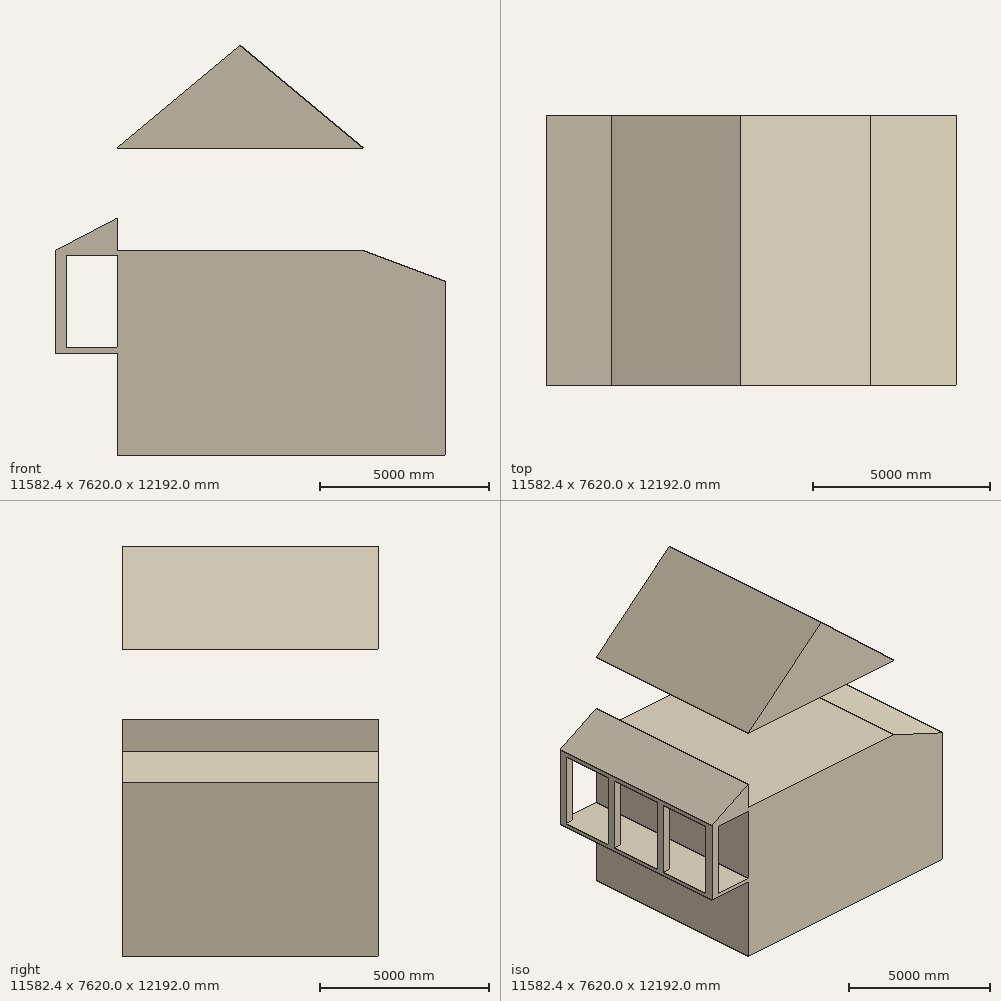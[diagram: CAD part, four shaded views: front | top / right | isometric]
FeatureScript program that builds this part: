
annotation { "Feature Type Name" : "Feature", "Feature Type Description" : "" }
export const myFeature = defineFeature(function(context is Context, id is Id, definition is map)
    precondition{}
    {
        {
            var Q0;
            Q0=qCreatedBy(makeId("Front.planeOp"),FACE);
            var sketch = newSketch(context, id + "F0", { "sketchPlane" : qUnion([Q0])});
            skLineSegment(sketch, "E0.bottom", {"start": v(0, 0) * mm, "end": v(-9753.6, 0) * mm});
            skLineSegment(sketch, "E0.top", {"start": v(0, 3048) * mm, "end": v(-9753.6, 3048) * mm});
            skLineSegment(sketch, "E0.left", {"start": v(0, 0) * mm, "end": v(0, 3048) * mm});
            skLineSegment(sketch, "E0.right", {"start": v(-9753.6, 0) * mm, "end": v(-9753.6, 3048) * mm});
            skLineSegment(sketch, "E1.bottom", {"start": v(0, 3048) * mm, "end": v(-11582.4, 3048) * mm});
            skLineSegment(sketch, "E1.top", {"start": v(-2438.33, 6096) * mm, "end": v(-9753.6, 6096) * mm});
            skLineSegment(sketch, "E1.left", {"start": v(0, 3048) * mm, "end": v(0, 5181.6) * mm});
            skLineSegment(sketch, "E1.right", {"start": v(-11582.4, 3048) * mm, "end": v(-11582.4, 6096) * mm});
            skLineSegment(sketch, "E2", {"start": v(0, 5181.6) * mm, "end": v(-2438.33, 6096) * mm});
            skLineSegment(sketch, "E3.bottom", {"start": v(-9753.6, 6096) * mm, "end": v(-2438.33, 6096) * mm});
            skLineSegment(sketch, "E3.top", {"start": v(-9753.6, 9144) * mm, "end": v(-2438.33, 9144) * mm});
            skLineSegment(sketch, "E3.left", {"start": v(-9753.6, 6096) * mm, "end": v(-9753.6, 9144) * mm});
            skLineSegment(sketch, "E3.right", {"start": v(-2438.33, 6096) * mm, "end": v(-2438.33, 9144) * mm});
            skLineSegment(sketch, "E4", {"start": v(-6095.96, 9144) * mm, "end": v(-6095.96, 12192) * mm});
            skLineSegment(sketch, "E5", {"start": v(-6095.96, 12192) * mm, "end": v(-2438.33, 9144) * mm});
            skLineSegment(sketch, "E6", {"start": v(-6095.96, 12192) * mm, "end": v(-9753.6, 9144) * mm});
            skLineSegment(sketch, "E7", {"start": v(-2438.33, 6096) * mm, "end": v(-2438.33, 6096) * mm});
            skLineSegment(sketch, "E8", {"start": v(-9753.6, 6096) * mm, "end": v(-11582.4, 6096) * mm});
            skLineSegment(sketch, "E9", {"start": v(-9753.6, 6096) * mm, "end": v(-9753.6, 7052.47) * mm});
            skLineSegment(sketch, "E10", {"start": v(-9753.6, 7052.47) * mm, "end": v(-11582.4, 6096) * mm});
            skSolve(sketch);
        }
        {
            var Q0;
            {var subQ2=sQuery(id+"F0.wireOp",EDGE,"E4");Q0=makeQuery(id+"F0.imprint","IMPRINT",FACE,{"disambiguationData":[TD([[makeQuery(id+"F0.imprint","IMPRINT",EDGE,{"derivedFrom":subQ2}),1.0]])]});}
            var Q1;
            Q1=makeQuery(id+"F0.imprint","IMPRINT",FACE,{"disambiguationData":[TD([[makeQuery(id+"F0.imprint","IMPRINT",EDGE,{"derivedFrom":sQuery(id+"F0.wireOp",EDGE,"E3.bottom")}),1.0]])]});
            var Q2;
            {var subQ1=sQuery(id+"F0.wireOp",EDGE,"E1.left");Q2=makeQuery(id+"F0.imprint","IMPRINT",FACE,{"disambiguationData":[TD([[makeQuery(id+"F0.imprint","IMPRINT",EDGE,{"derivedFrom":subQ1}),1.0]])]});}
            var Q3;
            Q3=makeQuery(id+"F0.imprint","IMPRINT",FACE,{"disambiguationData":[TD([[makeQuery(id+"F0.imprint","IMPRINT",EDGE,{"derivedFrom":sQuery(id+"F0.wireOp",EDGE,"E0.bottom")}),-1.0]])]});
            var Q4;
            {var subQ2=sQuery(id+"F0.wireOp",EDGE,"E4");Q4=makeQuery(id+"F0.imprint","IMPRINT",FACE,{"disambiguationData":[TD([[makeQuery(id+"F0.imprint","IMPRINT",EDGE,{"derivedFrom":subQ2}),-1.0]])]});}
            var Q5;
            Q5=makeQuery(id+"F0.imprint","IMPRINT",FACE,{"disambiguationData":[TD([[makeQuery(id+"F0.imprint","IMPRINT",EDGE,{"derivedFrom":sQuery(id+"F0.wireOp",EDGE,"E8")}),-1.0]])]});
            extrude(context, id + "F1", {"entities" : qUnion([Q0, Q1, Q2, Q3, Q4, Q5]), "depth" : 7620 * mm});
        }
        {
            var Q0;
            Q0=makeQuery(id+"F1.opExtrude","SWEPT_FACE",FACE,{"disambiguationData":[OSD([sQuery(id+"F0.wireOp",EDGE,"E1.right")])]});
            var sketch = newSketch(context, id + "F2", { "sketchPlane" : qUnion([Q0])});
            skLineSegment(sketch, "E11.bottom", {"start": v(304.8, 3200.4) * mm, "end": v(2438.4, 3200.4) * mm});
            skLineSegment(sketch, "E11.top", {"start": v(304.8, 5943.6) * mm, "end": v(2438.4, 5943.6) * mm});
            skLineSegment(sketch, "E11.left", {"start": v(304.8, 3200.4) * mm, "end": v(304.8, 5943.6) * mm});
            skLineSegment(sketch, "E11.right", {"start": v(2438.4, 3200.4) * mm, "end": v(2438.4, 5943.6) * mm});
            skLineSegment(sketch, "E12.bottom", {"start": v(2743.2, 5943.6) * mm, "end": v(4876.8, 5943.6) * mm});
            skLineSegment(sketch, "E12.top", {"start": v(2743.2, 3200.4) * mm, "end": v(4876.8, 3200.4) * mm});
            skLineSegment(sketch, "E12.left", {"start": v(2743.2, 5943.6) * mm, "end": v(2743.2, 3200.4) * mm});
            skLineSegment(sketch, "E12.right", {"start": v(4876.8, 5943.6) * mm, "end": v(4876.8, 3200.4) * mm});
            skLineSegment(sketch, "E13.bottom", {"start": v(5181.6, 5943.6) * mm, "end": v(7315.2, 5943.6) * mm});
            skLineSegment(sketch, "E13.top", {"start": v(5181.6, 3200.4) * mm, "end": v(7315.2, 3200.4) * mm});
            skLineSegment(sketch, "E13.left", {"start": v(5181.6, 5943.6) * mm, "end": v(5181.6, 3200.4) * mm});
            skLineSegment(sketch, "E13.right", {"start": v(7315.2, 5943.6) * mm, "end": v(7315.2, 3200.4) * mm});
            skSolve(sketch);
        }
        {
            var Q0;
            Q0=makeQuery(id+"F2.imprint","IMPRINT",FACE,{"disambiguationData":[TD([[makeQuery(id+"F2.imprint","IMPRINT",EDGE,{"derivedFrom":sQuery(id+"F2.wireOp",EDGE,"E11.bottom")}),1.0]])]});
            var Q1;
            Q1=makeQuery(id+"F2.imprint","IMPRINT",FACE,{"disambiguationData":[TD([[makeQuery(id+"F2.imprint","IMPRINT",EDGE,{"derivedFrom":sQuery(id+"F2.wireOp",EDGE,"E12.bottom")}),-1.0]])]});
            var Q2;
            Q2=makeQuery(id+"F2.imprint","IMPRINT",FACE,{"disambiguationData":[TD([[makeQuery(id+"F2.imprint","IMPRINT",EDGE,{"derivedFrom":sQuery(id+"F2.wireOp",EDGE,"E13.bottom")}),-1.0]])]});
            extrude(context, id + "F3", {"entities" : qUnion([Q0, Q1, Q2]), "operationType" : NewBodyOperationType.REMOVE, "oppositeDirection" : true, "depth" : 1828.8 * mm});
        }
        {
            var Q0;
            Q0=makeQuery(id+"F1.opExtrude","CAP_FACE",FACE,{"disambiguationData":[OSD([sQuery(id+"F0.wireOp",EDGE,"E0.bottom"),sQuery(id+"F0.wireOp",EDGE,"E0.left"),sQuery(id+"F0.wireOp",EDGE,"E0.right"),sQuery(id+"F0.wireOp",EDGE,"E1.bottom"),sQuery(id+"F0.wireOp",EDGE,"E1.left"),sQuery(id+"F0.wireOp",EDGE,"E1.right"),sQuery(id+"F0.wireOp",EDGE,"E2"),sQuery(id+"F0.wireOp",EDGE,"E3.left"),sQuery(id+"F0.wireOp",EDGE,"E3.right"),sQuery(id+"F0.wireOp",EDGE,"E5"),sQuery(id+"F0.wireOp",EDGE,"E6"),sQuery(id+"F0.wireOp",EDGE,"E10")])],"isStart":true});
            var sketch = newSketch(context, id + "F4", { "sketchPlane" : qUnion([Q0])});
            skLineSegment(sketch, "E14.bottom", {"start": v(9753.6, 3200.4) * mm, "end": v(11277.6, 3200.4) * mm});
            skLineSegment(sketch, "E14.top", {"start": v(9753.6, 5943.6) * mm, "end": v(11277.6, 5943.6) * mm});
            skLineSegment(sketch, "E14.left", {"start": v(9753.6, 3200.4) * mm, "end": v(9753.6, 5943.6) * mm});
            skLineSegment(sketch, "E14.right", {"start": v(11277.6, 3200.4) * mm, "end": v(11277.6, 5943.6) * mm});
            skSolve(sketch);
        }
        {
            var Q0;
            Q0=makeQuery(id+"F4.imprint","IMPRINT",FACE,{"disambiguationData":[TD([[makeQuery(id+"F4.imprint","IMPRINT",EDGE,{"derivedFrom":sQuery(id+"F4.wireOp",EDGE,"E14.bottom")}),1.0]])]});
            extrude(context, id + "F5", {"entities" : qUnion([Q0]), "operationType" : NewBodyOperationType.REMOVE, "oppositeDirection" : true, "depth" : 7620 * mm});
        }
    });
